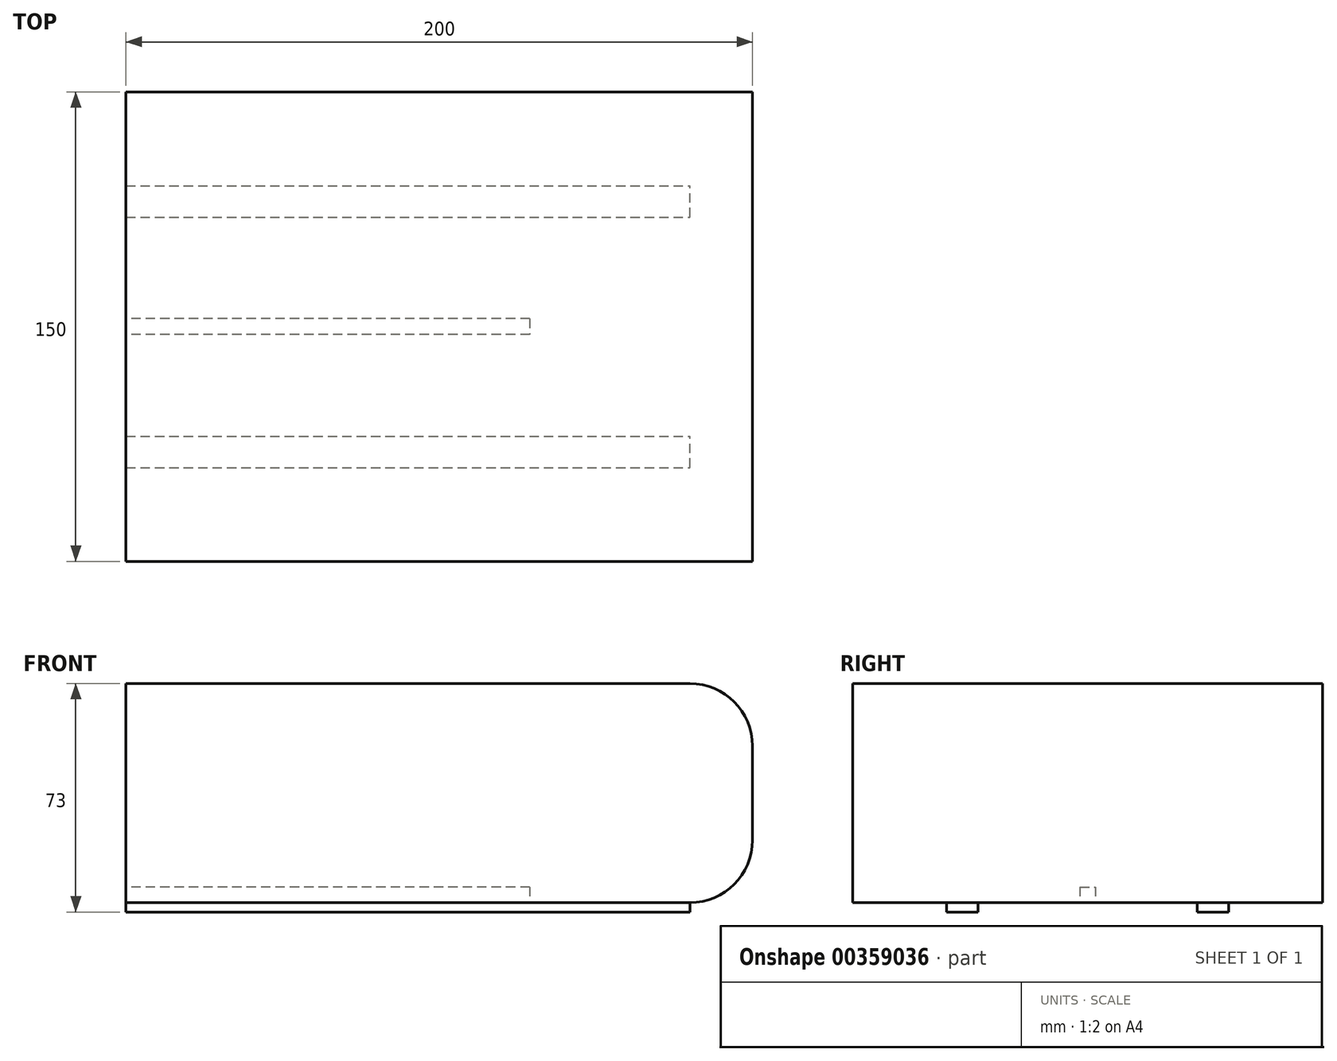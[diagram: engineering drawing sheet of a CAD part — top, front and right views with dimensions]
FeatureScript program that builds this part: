
annotation { "Feature Type Name" : "Feature", "Feature Type Description" : "" }
export const myFeature = defineFeature(function(context is Context, id is Id, definition is map)
    precondition{}
    {
        {
            var Q0;
            Q0=qCreatedBy(makeId("Front.planeOp"),FACE);
            var sketch = newSketch(context, id + "F0", { "sketchPlane" : qUnion([Q0])});
            skLineSegment(sketch, "E0.bottom", {"start": v(100, 35) * mm, "end": v(-100, 35) * mm});
            skLineSegment(sketch, "E0.top", {"start": v(100, -35) * mm, "end": v(-100, -35) * mm});
            skLineSegment(sketch, "E0.left", {"start": v(100, 35) * mm, "end": v(100, -35) * mm});
            skLineSegment(sketch, "E0.right", {"start": v(-100, 35) * mm, "end": v(-100, -35) * mm});
            skPoint(sketch, "E0.middle", {"position": v(0, 0) * mm});
            skSolve(sketch);
        }
        {
            var Q0;
            Q0=makeQuery(id+"F0.imprint","IMPRINT",FACE,{"disambiguationData":[TD([[makeQuery(id+"F0.imprint","IMPRINT",EDGE,{"derivedFrom":sQuery(id+"F0.wireOp",EDGE,"E0.bottom")}),1.0]])]});
            extrude(context, id + "F1", {"entities" : qUnion([Q0]), "endBound" : BoundingType.SYMMETRIC, "depth" : 150 * mm});
        }
        {
            var Q0;
            Q0=makeQuery(id+"F1.opExtrude","SWEPT_EDGE",EDGE,{"disambiguationData":[OSD([sQuery(id+"F0.wireOp",EDGE,"E0.bottom"),sQuery(id+"F0.wireOp",EDGE,"E0.left")])]});
            var Q1;
            Q1=makeQuery(id+"F1.opExtrude","SWEPT_EDGE",EDGE,{"disambiguationData":[OSD([sQuery(id+"F0.wireOp",EDGE,"E0.top"),sQuery(id+"F0.wireOp",EDGE,"E0.left")])]});
            fillet(context, id + "F2", {"entities" : qUnion([Q0, Q1]), "radius" : 20 * mm, "tangentPropagation" : true, "rho" : 0, "crossSection" : FilletCrossSection.CONIC, "allowEdgeOverflow" : false});
        }
        {
            var Q0;
            Q0=makeQuery(id+"F1.opExtrude","SWEPT_FACE",FACE,{"disambiguationData":[OSD([sQuery(id+"F0.wireOp",EDGE,"E0.top")])]});
            var sketch = newSketch(context, id + "F3", { "sketchPlane" : qUnion([Q0])});
            skLineSegment(sketch, "E1", {"start": v(-73.65, 75) * mm, "end": v(-73.65, 45) * mm});
            skLineSegment(sketch, "E2", {"start": v(-73.65, -75) * mm, "end": v(-73.65, -45) * mm});
            skLineSegment(sketch, "E3.bottom", {"start": v(-100, -45) * mm, "end": v(80, -45) * mm});
            skLineSegment(sketch, "E3.top", {"start": v(-100, -35) * mm, "end": v(80, -35) * mm});
            skLineSegment(sketch, "E3.left", {"start": v(-100, -45) * mm, "end": v(-100, -35) * mm});
            skLineSegment(sketch, "E3.right", {"start": v(80, -45) * mm, "end": v(80, -35) * mm});
            skPoint(sketch, "E4.firstSnap0", {"position": v(-100, 0) * mm});
            skLineSegment(sketch, "E4.bottom", {"start": v(-100, 45) * mm, "end": v(80, 45) * mm});
            skLineSegment(sketch, "E4.top", {"start": v(-100, 35) * mm, "end": v(80, 35) * mm});
            skLineSegment(sketch, "E4.left", {"start": v(-100, 45) * mm, "end": v(-100, 35) * mm});
            skLineSegment(sketch, "E4.right", {"start": v(80, 45) * mm, "end": v(80, 35) * mm});
            skSolve(sketch);
        }
        {
            var Q0;
            Q0=makeQuery(id+"F3.imprint","IMPRINT",FACE,{"disambiguationData":[TD([[makeQuery(id+"F3.imprint","IMPRINT",EDGE,{"derivedFrom":sQuery(id+"F3.wireOp",EDGE,"E4.top")}),1.0]])]});
            extrude(context, id + "F4", {"entities" : qUnion([Q0]), "operationType" : NewBodyOperationType.ADD, "depth" : 3 * mm});
        }
        {
            var Q0;
            {var subQ1=sQuery(id+"F0.wireOp",EDGE,"E0.top");Q0=makeQuery(id+"F4.boolean.opBoolean","SPLIT",FACE,{"disambiguationData":[TD([makeQuery(id+"F4.opExtrude","SWEPT_FACE",FACE,{"disambiguationData":[OSD([sQuery(id+"F3.wireOp",EDGE,"E4.top")])]})])],"derivedFrom":makeQuery(id+"F1.opExtrude","SWEPT_FACE",FACE,{"disambiguationData":[OSD([subQ1])]})});}
            var sketch = newSketch(context, id + "F5", { "sketchPlane" : qUnion([Q0])});
            skLineSegment(sketch, "E5", {"start": v(-63.58, -75) * mm, "end": v(-63.58, -45) * mm});
            skLineSegment(sketch, "E6", {"start": v(-100, -45) * mm, "end": v(80, -45) * mm});
            skLineSegment(sketch, "E7.top", {"start": v(-100, -35) * mm, "end": v(80, -35) * mm});
            skLineSegment(sketch, "E7.left", {"start": v(-100, -45) * mm, "end": v(-100, -35) * mm});
            skLineSegment(sketch, "E7.right", {"start": v(80, -45) * mm, "end": v(80, -35) * mm});
            skSolve(sketch);
        }
        {
            var Q0;
            Q0=makeQuery(id+"F5.imprint","IMPRINT",FACE,{"disambiguationData":[TD([[makeQuery(id+"F5.imprint","IMPRINT",EDGE,{"derivedFrom":sQuery(id+"F5.wireOp",EDGE,"E7.top")}),-1.0]])]});
            extrude(context, id + "F6", {"entities" : qUnion([Q0]), "operationType" : NewBodyOperationType.ADD, "depth" : 3 * mm});
        }
        {
            var Q0;
            {var subQ1=makeQuery(id+"F4.opExtrude","SWEPT_FACE",FACE,{"disambiguationData":[OSD([sQuery(id+"F3.wireOp",EDGE,"E4.top")])]});var subQ3=sQuery(id+"F0.wireOp",EDGE,"E0.top");Q0=makeQuery(id+"F6.boolean.opBoolean","SPLIT",FACE,{"disambiguationData":[TD([subQ1])],"derivedFrom":makeQuery(id+"F4.boolean.opBoolean","SPLIT",FACE,{"disambiguationData":[TD([subQ1])],"derivedFrom":makeQuery(id+"F1.opExtrude","SWEPT_FACE",FACE,{"disambiguationData":[OSD([subQ3])]})})});}
            var sketch = newSketch(context, id + "F7", { "sketchPlane" : qUnion([Q0])});
            skLineSegment(sketch, "E8", {"start": v(28.87, 0) * mm, "end": v(28.87, -2.5) * mm});
            skLineSegment(sketch, "E9", {"start": v(28.87, 0) * mm, "end": v(28.87, 2.5) * mm});
            skLineSegment(sketch, "E10.bottom", {"start": v(28.87, 2.5) * mm, "end": v(-100, 2.5) * mm});
            skLineSegment(sketch, "E10.top", {"start": v(28.87, -2.5) * mm, "end": v(-100, -2.5) * mm});
            skLineSegment(sketch, "E10.left", {"start": v(28.87, 2.5) * mm, "end": v(28.87, -2.5) * mm});
            skLineSegment(sketch, "E10.right", {"start": v(-100, 2.5) * mm, "end": v(-100, -2.5) * mm});
            skSolve(sketch);
        }
        {
            var Q0;
            Q0=makeQuery(id+"F7.imprint","IMPRINT",FACE,{"disambiguationData":[TD([[makeQuery(id+"F7.imprint","IMPRINT",EDGE,{"derivedFrom":sQuery(id+"F7.wireOp",EDGE,"E10.bottom")}),1.0]])]});
            extrude(context, id + "F8", {"entities" : qUnion([Q0]), "operationType" : NewBodyOperationType.REMOVE, "oppositeDirection" : true, "depth" : 5 * mm});
        }
    });
